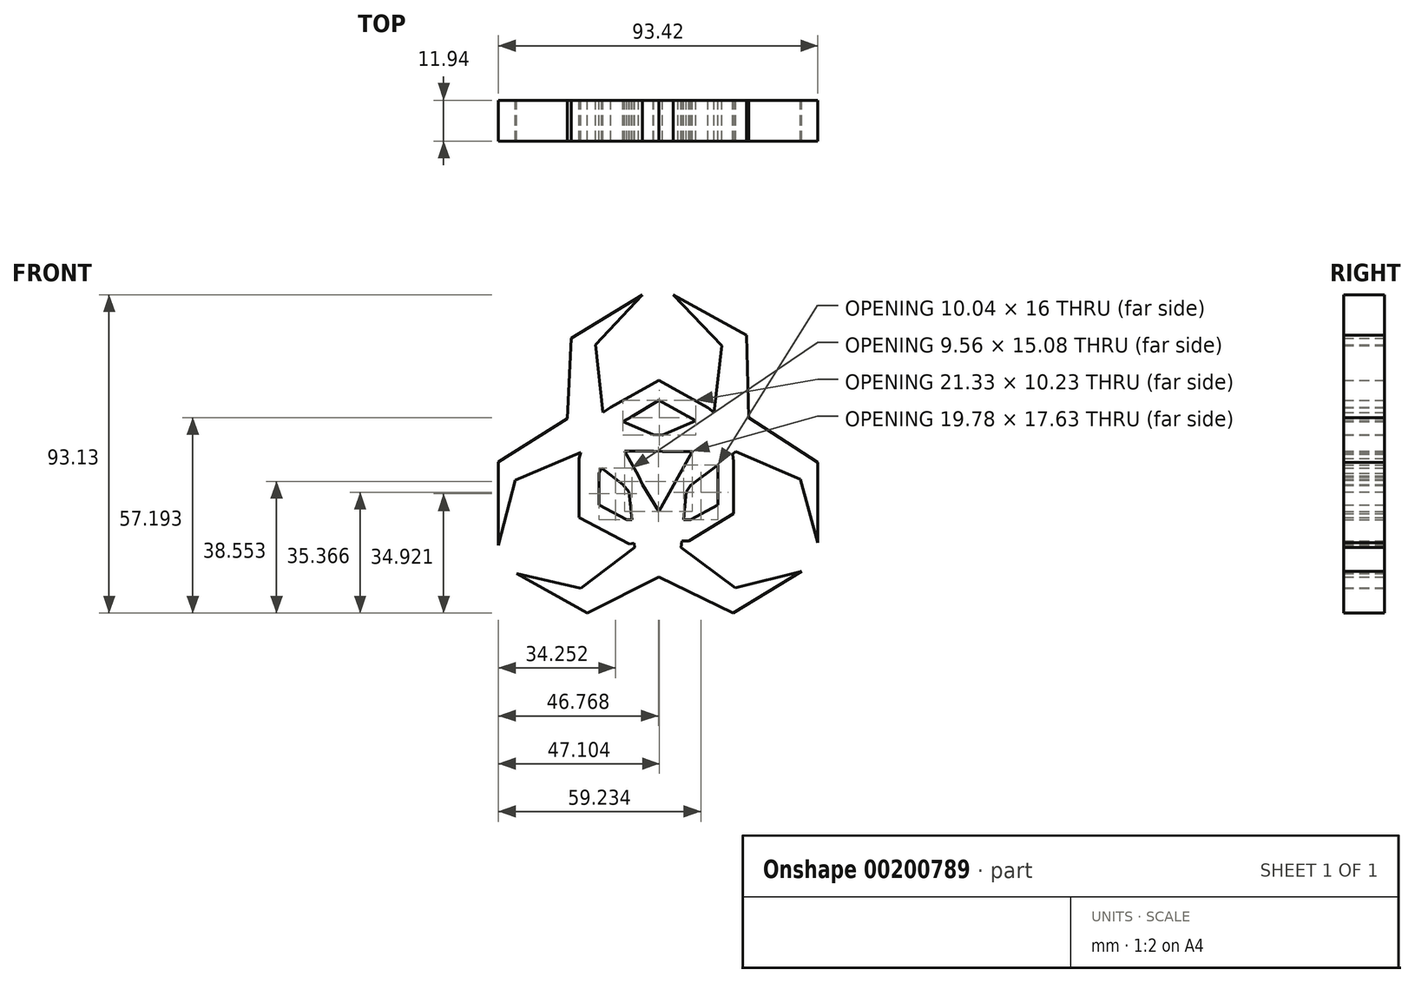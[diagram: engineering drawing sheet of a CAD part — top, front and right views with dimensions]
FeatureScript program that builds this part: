
annotation { "Feature Type Name" : "Feature", "Feature Type Description" : "" }
export const myFeature = defineFeature(function(context is Context, id is Id, definition is map)
    precondition{}
    {
        {
            var Q0;
            Q0=qCreatedBy(makeId("Front.planeOp"),FACE);
            var sketch = newSketch(context, id + "F0", { "sketchPlane" : qUnion([Q0])});
            skLineSegment(sketch, "E0", {"start": v(-10.1, 4.5) * mm, "end": v(-6.06, -2.62) * mm});
            skLineSegment(sketch, "E1", {"start": v(-10.1, 4.5) * mm, "end": v(-1.48, 4.5) * mm});
            skLineSegment(sketch, "E2", {"start": v(0.94, 4.37) * mm, "end": v(9.7, 4.37) * mm});
            skLineSegment(sketch, "E3", {"start": v(9.7, 4.37) * mm, "end": v(5.52, -3.03) * mm});
            skLineSegment(sketch, "E4", {"start": v(0, -13.12) * mm, "end": v(-4.85, -5.18) * mm});
            skLineSegment(sketch, "E5", {"start": v(0, -13.12) * mm, "end": v(4.3, -5.32) * mm});
            skLineSegment(sketch, "E6", {"start": v(8.03, -7.37) * mm, "end": v(6.46, -23.62) * mm});
            skLineSegment(sketch, "E7", {"start": v(6.46, -23.62) * mm, "end": v(22.34, -35.46) * mm});
            skLineSegment(sketch, "E8", {"start": v(22.34, -35.46) * mm, "end": v(41.72, -30.62) * mm});
            skLineSegment(sketch, "E9", {"start": v(41.72, -30.62) * mm, "end": v(21.65, -42.86) * mm});
            skLineSegment(sketch, "E10", {"start": v(21.65, -42.86) * mm, "end": v(0, -32.23) * mm});
            skLineSegment(sketch, "E11", {"start": v(0, -32.23) * mm, "end": v(-21, -42.86) * mm});
            skLineSegment(sketch, "E12", {"start": v(-21, -42.86) * mm, "end": v(-41.61, -31.24) * mm});
            skLineSegment(sketch, "E13", {"start": v(-41.61, -31.24) * mm, "end": v(-22.88, -35.6) * mm});
            skLineSegment(sketch, "E14", {"start": v(-22.88, -35.6) * mm, "end": v(-7.13, -23.62) * mm});
            skLineSegment(sketch, "E15", {"start": v(-7.13, -23.62) * mm, "end": v(-8.75, -7.33) * mm});
            skLineSegment(sketch, "E16", {"start": v(-10.57, -5.18) * mm, "end": v(-22.88, 4.24) * mm});
            skLineSegment(sketch, "E17", {"start": v(-22.88, 4.24) * mm, "end": v(-42.12, -3.97) * mm});
            skLineSegment(sketch, "E18", {"start": v(-42.12, -3.97) * mm, "end": v(-46.97, -22.95) * mm});
            skLineSegment(sketch, "E19", {"start": v(-46.97, -22.95) * mm, "end": v(-46.97, 1.41) * mm});
            skLineSegment(sketch, "E20", {"start": v(-46.97, 1.41) * mm, "end": v(-26.78, 14.06) * mm});
            skLineSegment(sketch, "E21", {"start": v(-26.78, 14.06) * mm, "end": v(-25.7, 37.62) * mm});
            skLineSegment(sketch, "E22", {"start": v(-25.7, 37.62) * mm, "end": v(-4.85, 50.27) * mm});
            skLineSegment(sketch, "E23", {"start": v(-4.85, 50.27) * mm, "end": v(-18.57, 35.73) * mm});
            skLineSegment(sketch, "E24", {"start": v(-18.57, 35.73) * mm, "end": v(-16.42, 15.81) * mm});
            skLineSegment(sketch, "E25", {"start": v(-16.42, 15.81) * mm, "end": v(-1.62, 9.35) * mm});
            skLineSegment(sketch, "E26", {"start": v(0.94, 9.22) * mm, "end": v(16.15, 15.81) * mm});
            skLineSegment(sketch, "E27", {"start": v(16.15, 15.81) * mm, "end": v(18.44, 35.46) * mm});
            skLineSegment(sketch, "E28", {"start": v(18.44, 35.46) * mm, "end": v(4.17, 50.27) * mm});
            skLineSegment(sketch, "E29", {"start": v(4.17, 50.27) * mm, "end": v(25.57, 38.42) * mm});
            skLineSegment(sketch, "E30", {"start": v(25.57, 38.42) * mm, "end": v(26.24, 14.33) * mm});
            skLineSegment(sketch, "E31", {"start": v(26.24, 14.33) * mm, "end": v(46.45, 1.28) * mm});
            skLineSegment(sketch, "E32", {"start": v(46.45, 1.28) * mm, "end": v(46.45, -22.27) * mm});
            skLineSegment(sketch, "E33", {"start": v(46.45, -22.27) * mm, "end": v(41.32, -3.7) * mm});
            skLineSegment(sketch, "E34", {"start": v(41.32, -3.7) * mm, "end": v(22.48, 4.37) * mm});
            skLineSegment(sketch, "E35", {"start": v(22.48, 4.37) * mm, "end": v(9.29, -5.45) * mm});
            skLineSegment(sketch, "E36", {"start": v(-17.5, -1.95) * mm, "end": v(-17.5, -11.24) * mm});
            skLineSegment(sketch, "E37", {"start": v(-17.5, -11.24) * mm, "end": v(-9.42, -15.48) * mm});
            skPoint(sketch, "E37.endSnap0", {"position": v(-7.94, -15.48) * mm});
            skLineSegment(sketch, "E38", {"start": v(-8.72, -22.55) * mm, "end": v(-23.42, -14.87) * mm});
            skLineSegment(sketch, "E39", {"start": v(-23.42, -14.87) * mm, "end": v(-23.42, 2.36) * mm});
            skPoint(sketch, "E40.startSnap0", {"position": v(7.24, -15.5) * mm});
            skLineSegment(sketch, "E41", {"start": v(8.68, -21.78) * mm, "end": v(21.79, -13.78) * mm});
            skLineSegment(sketch, "E42", {"start": v(21.79, -13.78) * mm, "end": v(21.79, 1.55) * mm});
            skLineSegment(sketch, "E43", {"start": v(17.28, -1.2) * mm, "end": v(17.28, -11.24) * mm});
            skPoint(sketch, "E44.startSnap0", {"position": v(8.55, 12.52) * mm});
            skLineSegment(sketch, "E45", {"start": v(14.3, 17.23) * mm, "end": v(0, 25.23) * mm});
            skLineSegment(sketch, "E46", {"start": v(0, 25.23) * mm, "end": v(-14.13, 17.43) * mm});
            skLineSegment(sketch, "E47", {"start": v(-8.08, 14.6) * mm, "end": v(0, 19.45) * mm});
            skLineSegment(sketch, "E48", {"start": v(0, 19.45) * mm, "end": v(8.55, 14.74) * mm});
            skPoint(sketch, "E40.start.orphan", {"position": v(9.29, -15.5) * mm});
            skLineSegment(sketch, "E49", {"start": v(-9.42, -15.48) * mm, "end": v(-7.94, -15.48) * mm});
            skLineSegment(sketch, "E50", {"start": v(-8.72, -22.55) * mm, "end": v(-7.13, -22.4) * mm});
            skLineSegment(sketch, "E51", {"start": v(-23.42, 2.36) * mm, "end": v(-22.88, 4.24) * mm});
            skLineSegment(sketch, "E52", {"start": v(-17.5, -1.95) * mm, "end": v(-16.73, -0.19) * mm});
            skPoint(sketch, "E52.endSnap0", {"position": v(-16.73, -0.47) * mm});
            skLineSegment(sketch, "E53", {"start": v(9.29, -15.5) * mm, "end": v(7.24, -15.5) * mm});
            skLineSegment(sketch, "E54", {"start": v(8.68, -21.78) * mm, "end": v(6.65, -21.69) * mm});
            skLineSegment(sketch, "E55", {"start": v(17.28, -1.2) * mm, "end": v(17.28, 0.5) * mm});
            skLineSegment(sketch, "E56", {"start": v(21.79, 1.55) * mm, "end": v(21.56, 3.69) * mm});
            skLineSegment(sketch, "E57", {"start": v(-14.13, 17.43) * mm, "end": v(-16.42, 15.81) * mm});
            skLineSegment(sketch, "E58", {"start": v(-8.08, 14.6) * mm, "end": v(-10.53, 13.24) * mm});
            skLineSegment(sketch, "E59", {"start": v(8.55, 14.74) * mm, "end": v(10.8, 13.5) * mm});
            skLineSegment(sketch, "E60", {"start": v(14.3, 17.23) * mm, "end": v(16.15, 15.81) * mm});
            skLineSegment(sketch, "E61", {"start": v(-6.06, -2.62) * mm, "end": v(-4.85, -5.18) * mm});
            skLineSegment(sketch, "E62", {"start": v(-10.57, -5.18) * mm, "end": v(-8.75, -7.33) * mm});
            skLineSegment(sketch, "E63", {"start": v(0.94, 9.22) * mm, "end": v(-1.62, 9.35) * mm});
            skLineSegment(sketch, "E64", {"start": v(-1.48, 4.5) * mm, "end": v(0.94, 4.37) * mm});
            skLineSegment(sketch, "E65", {"start": v(5.52, -3.03) * mm, "end": v(4.3, -5.32) * mm});
            skLineSegment(sketch, "E66", {"start": v(9.29, -5.45) * mm, "end": v(8.03, -7.37) * mm});
            skLineSegment(sketch, "E67", {"start": v(9.29, -15.5) * mm, "end": v(17.28, -11.24) * mm});
            skSolve(sketch);
        }
        {
            var Q0;
            Q0 = qSketchRegion(id + "F0", true);
            extrude(context, id + "F1", {"entities" : qUnion([Q0]), "depth" : 11.94 * mm});
        }
    });
